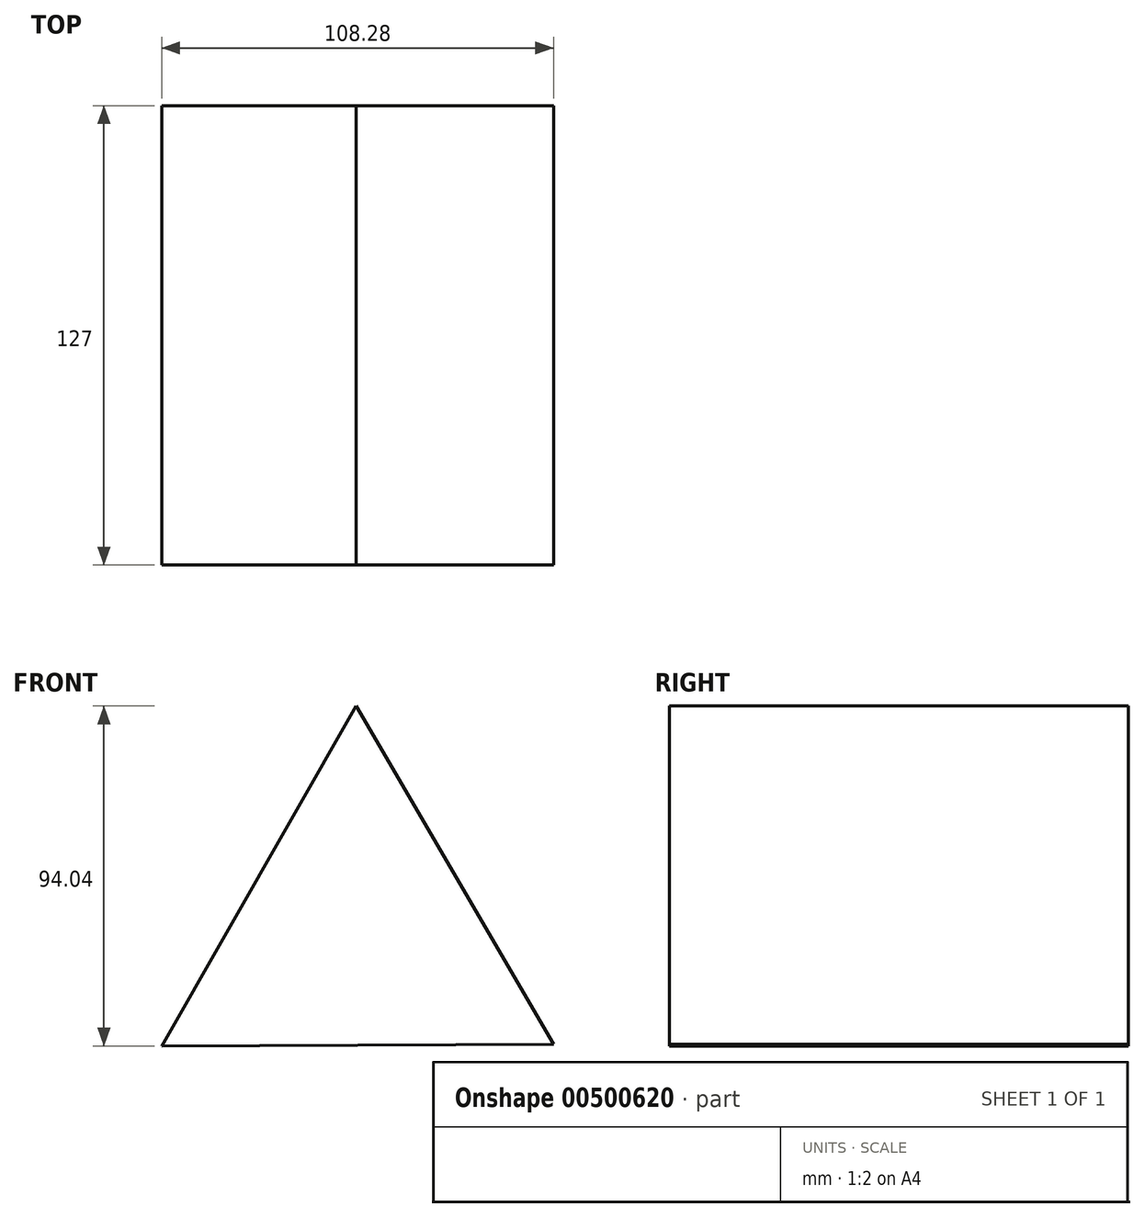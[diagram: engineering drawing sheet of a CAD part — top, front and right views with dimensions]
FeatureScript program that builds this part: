
annotation { "Feature Type Name" : "Feature", "Feature Type Description" : "" }
export const myFeature = defineFeature(function(context is Context, id is Id, definition is map)
    precondition{}
    {
        {
            var Q0;
            Q0=qCreatedBy(makeId("Front.planeOp"),FACE);
            var sketch = newSketch(context, id + "F0", { "sketchPlane" : qUnion([Q0])});
            skCircle(sketch, "E0.cCircle", {"center": v(0, 0) * mm, "radius": 62.52 * mm, "construction": true});
            skLineSegment(sketch, "E0.0", {"start": v(-0.3, 62.52) * mm, "end": v(54.3, -31) * mm});
            skLineSegment(sketch, "E0.1", {"start": v(54.3, -31) * mm, "end": v(-54, -31.52) * mm});
            skLineSegment(sketch, "E0.2", {"start": v(-54, -31.52) * mm, "end": v(-0.3, 62.52) * mm});
            skSolve(sketch);
        }
        {
            var Q0;
            Q0=makeQuery(id+"F0.imprint","IMPRINT",FACE,{"disambiguationData":[TD([[makeQuery(id+"F0.imprint","IMPRINT",EDGE,{"derivedFrom":sQuery(id+"F0.wireOp",EDGE,"E0.0")}),-1.0]])]});
            extrude(context, id + "F1", {"entities" : qUnion([Q0]), "depth" : 127 * mm});
        }
    });
